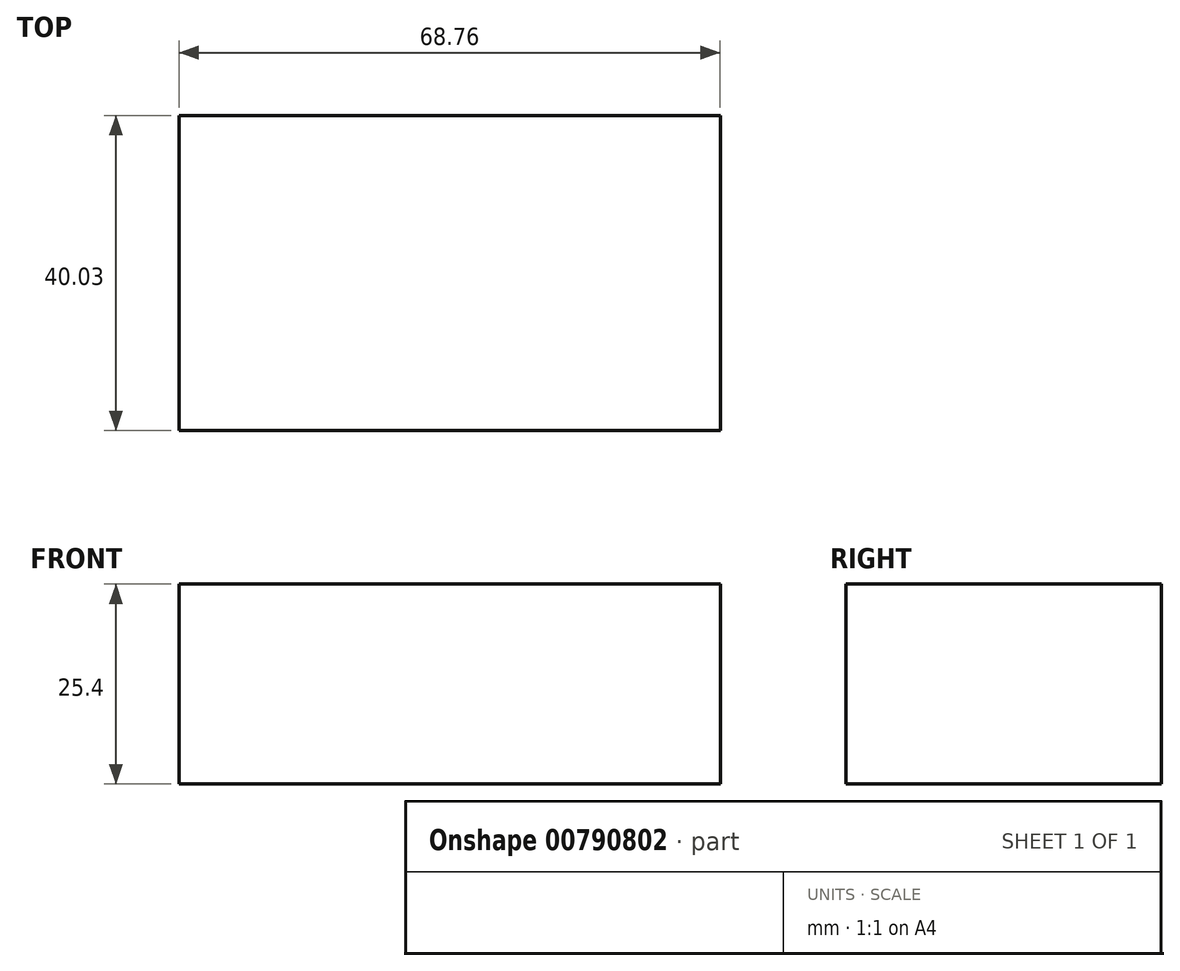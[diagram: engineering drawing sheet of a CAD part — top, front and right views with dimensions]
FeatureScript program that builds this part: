
annotation { "Feature Type Name" : "Feature", "Feature Type Description" : "" }
export const myFeature = defineFeature(function(context is Context, id is Id, definition is map)
    precondition{}
    {
        {
            var Q0;
            Q0=qCreatedBy(makeId("Top.planeOp"),FACE);
            var sketch = newSketch(context, id + "F0", { "sketchPlane" : qUnion([Q0])});
            skLineSegment(sketch, "E0.bottom", {"start": v(-113.68, 0) * mm, "end": v(-44.92, 0) * mm});
            skLineSegment(sketch, "E0.top", {"start": v(-113.68, 40.03) * mm, "end": v(-44.92, 40.03) * mm});
            skLineSegment(sketch, "E0.left", {"start": v(-113.68, 0) * mm, "end": v(-113.68, 40.03) * mm});
            skLineSegment(sketch, "E0.right", {"start": v(-44.92, 0) * mm, "end": v(-44.92, 40.03) * mm});
            skSolve(sketch);
        }
        {
            var Q0;
            Q0=makeQuery(id+"F0.imprint","IMPRINT",FACE,{"disambiguationData":[TD([[makeQuery(id+"F0.imprint","IMPRINT",EDGE,{"derivedFrom":sQuery(id+"F0.wireOp",EDGE,"E0.bottom")}),1.0]])]});
            extrude(context, id + "F1", {"entities" : qUnion([Q0]), "depth" : 25.4 * mm, "offsetDistance" : 25.4 * mm});
        }
    });
